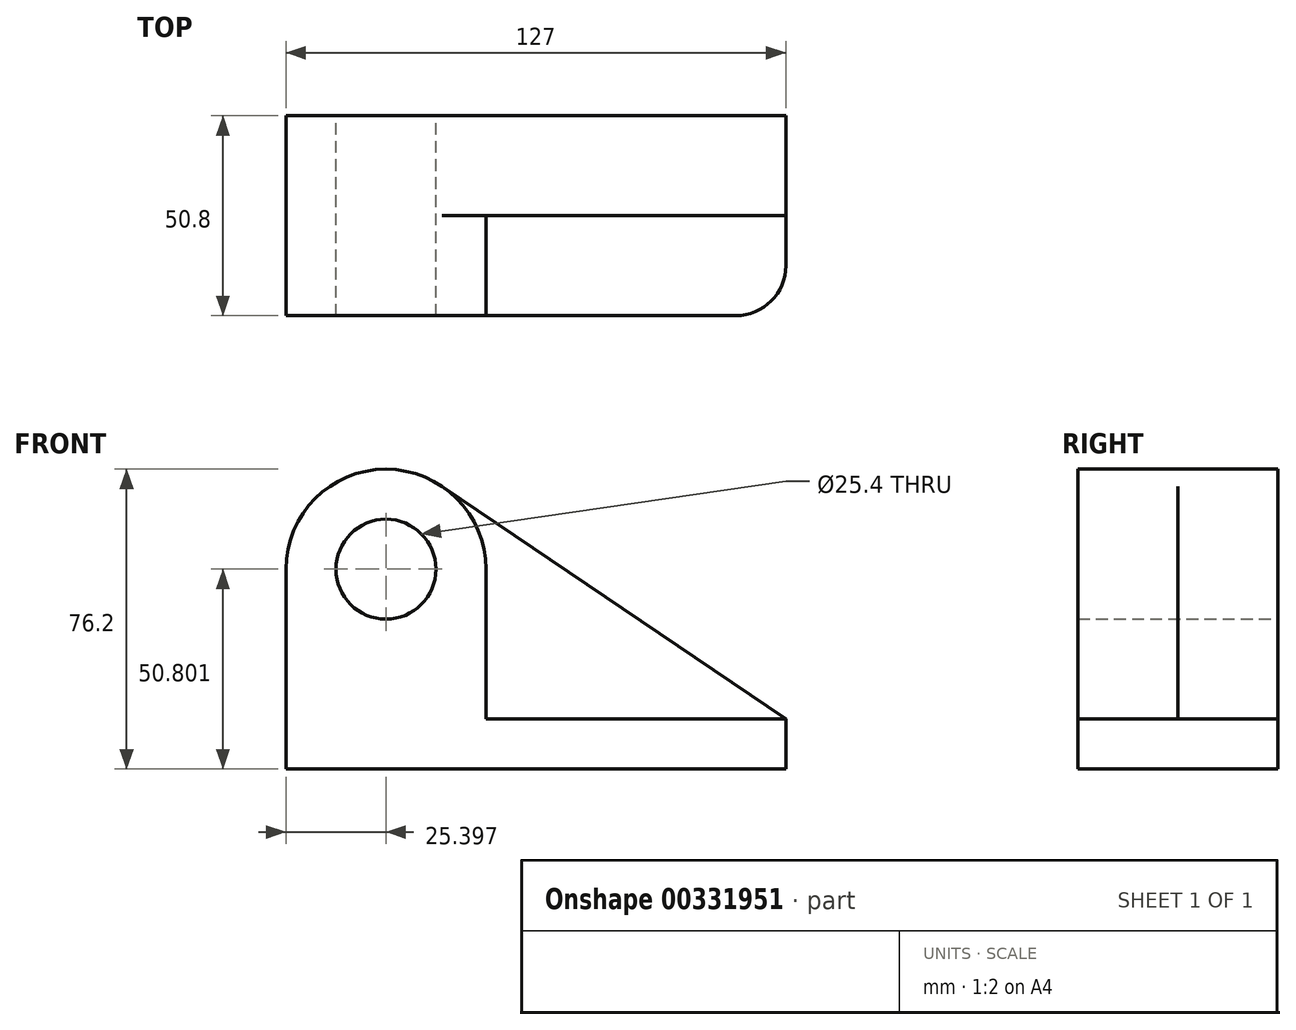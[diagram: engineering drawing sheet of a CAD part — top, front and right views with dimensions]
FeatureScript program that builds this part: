
annotation { "Feature Type Name" : "Feature", "Feature Type Description" : "" }
export const myFeature = defineFeature(function(context is Context, id is Id, definition is map)
    precondition{}
    {
        {
            var Q0;
            Q0=qCreatedBy(makeId("Front.planeOp"),FACE);
            var sketch = newSketch(context, id + "F0", { "sketchPlane" : qUnion([Q0])});
            skCircle(sketch, "E0", {"center": v(-36.27, 15.3) * mm, "radius": 12.7 * mm});
            skArc(sketch, "E1", {"start": v(-22.03, 36.33) * mm, "mid": v(-48.18, 37.73) * mm, "end": v(-61.67, 15.3) * mm});
            skLineSegment(sketch, "E2", {"start": v(-61.67, 15.3) * mm, "end": v(-61.67, -35.5) * mm});
            skLineSegment(sketch, "E3", {"start": v(-61.67, -35.5) * mm, "end": v(65.33, -35.5) * mm});
            skLineSegment(sketch, "E4", {"start": v(65.33, -35.5) * mm, "end": v(65.33, -22.8) * mm});
            skLineSegment(sketch, "E5", {"start": v(65.33, -22.8) * mm, "end": v(-22.03, 36.33) * mm});
            skSolve(sketch);
        }
        {
            var Q0;
            Q0=makeQuery(id+"F0.imprint","IMPRINT",FACE,{"disambiguationData":[TD([[makeQuery(id+"F0.imprint","IMPRINT",EDGE,{"derivedFrom":sQuery(id+"F0.wireOp",EDGE,"E0")}),-1.0]])]});
            extrude(context, id + "F1", {"entities" : qUnion([Q0]), "depth" : 25.4 * mm});
        }
        {
            var Q0;
            Q0=makeQuery(id+"F1.opExtrude","CAP_FACE",FACE,{"disambiguationData":[OSD([sQuery(id+"F0.wireOp",EDGE,"E0"),sQuery(id+"F0.wireOp",EDGE,"E1"),sQuery(id+"F0.wireOp",EDGE,"E2"),sQuery(id+"F0.wireOp",EDGE,"E3"),sQuery(id+"F0.wireOp",EDGE,"E4"),sQuery(id+"F0.wireOp",EDGE,"E5")])],"isStart":false});
            var sketch = newSketch(context, id + "F2", { "sketchPlane" : qUnion([Q0])});
            skCircle(sketch, "E6", {"center": v(-36.27, 15.3) * mm, "radius": 12.7 * mm});
            skArc(sketch, "E7", {"start": v(-10.87, 15.3) * mm, "mid": v(-38.28, 40.61) * mm, "end": v(-61.36, 11.3) * mm});
            skLineSegment(sketch, "E8.bottom", {"start": v(65.33, -22.8) * mm, "end": v(-10.87, -22.8) * mm});
            skLineSegment(sketch, "E8.top", {"start": v(65.33, -35.5) * mm, "end": v(-61.67, -35.5) * mm});
            skLineSegment(sketch, "E8.left", {"start": v(65.33, -22.8) * mm, "end": v(65.33, -35.5) * mm});
            skLineSegment(sketch, "E8.right", {"start": v(-61.67, -22.8) * mm, "end": v(-61.67, -35.5) * mm});
            skLineSegment(sketch, "E9", {"start": v(-10.87, 15.3) * mm, "end": v(-10.87, -22.8) * mm});
            skSolve(sketch);
        }
        {
            var Q0;
            Q0=makeQuery(id+"F2.imprint","IMPRINT",FACE,{"disambiguationData":[TD([[makeQuery(id+"F2.imprint","IMPRINT",EDGE,{"derivedFrom":sQuery(id+"F2.wireOp",EDGE,"E6")}),-1.0]])]});
            extrude(context, id + "F3", {"entities" : qUnion([Q0]), "operationType" : NewBodyOperationType.ADD, "depth" : 25.4 * mm});
        }
        {
            var Q0;
            Q0=makeQuery(id+"F3.opExtrude","CAP_EDGE",EDGE,{"disambiguationData":[OSD([sQuery(id+"F2.wireOp",EDGE,"E8.left")])],"isStart":false});
            fillet(context, id + "F4", {"entities" : qUnion([Q0]), "radius" : 12.7 * mm, "tangentPropagation" : true, "allowEdgeOverflow" : false});
        }
    });
